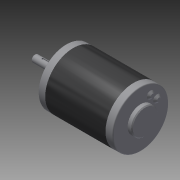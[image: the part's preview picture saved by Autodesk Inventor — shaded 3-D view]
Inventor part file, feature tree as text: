
AUTODESK INVENTOR PART (.ipt)
format: ipt  version: 2013 SP1 (Build 170176100, 176)  size: 152,576 bytes
history: native  units: in
note: dims shown in document units (in); Inventor stores cm internally (conversion verified against a paired STEP export)
features: chamfer x1, imported_body x1
ambient origin geometry x8: Origin, YZ Plane, XZ Plane, XY Plane, X Axis, Y Axis, Z Axis, Center Point
feature tree (2):
  chamfer  "Chamfer3"  [1 undecoded]
  imported_body  "Base1"
note: 1 required parameter value undecoded (feature->parameter linkage not recoverable at this tier; creation-order binding heuristic only, values carry confidence <= 0.55)
